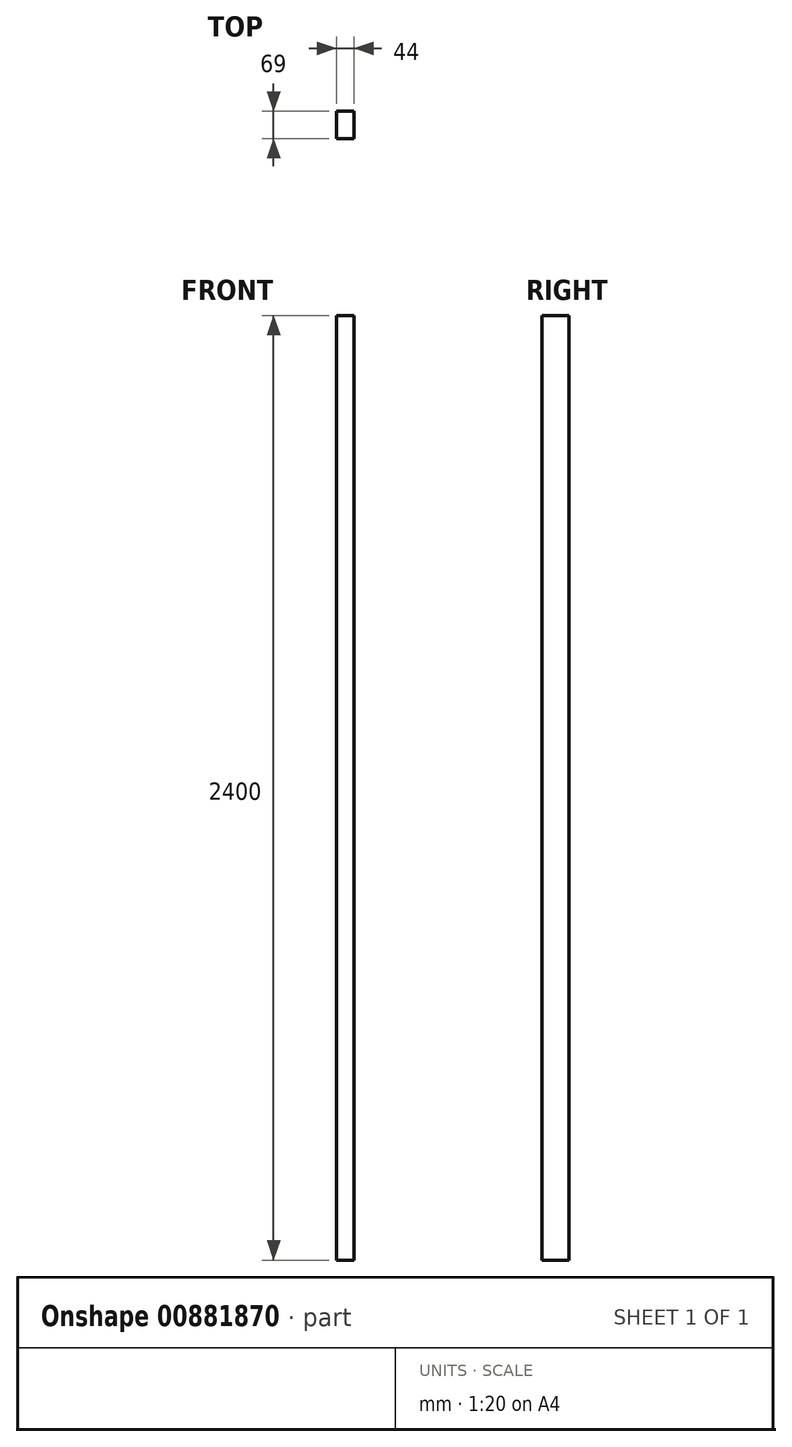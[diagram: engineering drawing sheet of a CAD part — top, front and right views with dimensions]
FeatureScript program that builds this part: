
annotation { "Feature Type Name" : "Feature", "Feature Type Description" : "" }
export const myFeature = defineFeature(function(context is Context, id is Id, definition is map)
    precondition{}
    {
        {
            var Q0;
            Q0=qCreatedBy(makeId("Top.planeOp"),FACE);
            var sketch = newSketch(context, id + "F0", { "sketchPlane" : qUnion([Q0])});
            skLineSegment(sketch, "E0.bottom", {"start": v(22, -34.5) * mm, "end": v(-22, -34.5) * mm});
            skLineSegment(sketch, "E0.top", {"start": v(22, 34.5) * mm, "end": v(-22, 34.5) * mm});
            skLineSegment(sketch, "E0.left", {"start": v(22, -34.5) * mm, "end": v(22, 34.5) * mm});
            skLineSegment(sketch, "E0.right", {"start": v(-22, -34.5) * mm, "end": v(-22, 34.5) * mm});
            skPoint(sketch, "E0.middle", {"position": v(0, 0) * mm});
            skSolve(sketch);
        }
        {
            var Q0;
            Q0=qSketchRegion(id+"F0",true);
            extrude(context, id + "F1", {"entities" : qUnion([Q0]), "depth" : 2400 * mm, "offsetDistance" : 25 * mm});
        }
    });
